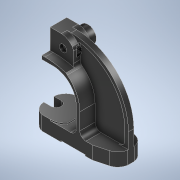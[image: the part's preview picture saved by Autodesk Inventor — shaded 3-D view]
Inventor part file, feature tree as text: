
AUTODESK INVENTOR PART (.ipt)
format: ipt  version: 2021 (Build 250183000, 183)  size: 490,496 bytes
history: native  units: in
note: dims shown in document units (in); Inventor stores cm internally (conversion verified against a paired STEP export)
features: sketch x18, extrude x17, mirror x3, fillet x3, plane x1, hole x1, projected_geometry x1
ambient origin geometry x8: Origin, YZ Plane, XZ Plane, XY Plane, X Axis, Y Axis, Z Axis, Center Point
bodies: Solid1 (feature_tree)
feature tree (44):
  extrude  "Extrusion1"  Depth=1.5in
  extrude  "Extrusion2"  Depth=2.5in
  extrude  "Extrusion3"  Depth=9.0in
  extrude  "Extrusion4"  Depth=0.125in
  extrude  "Extrusion5"  Depth=1.5in
  plane  "Work Plane1"
  mirror  "Mirror1"
  extrude  "Extrusion6"  Depth=3.5in TaperAngle=0.0deg
  extrude  "Extrusion7"  TaperAngle=15.0deg  [1 undecoded]
  extrude  "Extrusion8"  TaperAngle=0.0deg  [1 undecoded]
  extrude  "Extrusion9"  Depth=2.434in
  extrude  "Extrusion10"  Depth=3.375in
  extrude  "Extrusion11"  Depth=0.375in
  mirror  "Mirror2"
  fillet  "Fillet1"  Radius=0.125in
  extrude  "Extrusion12"  Depth=0.375in
  extrude  "Extrusion13"  Depth=0.875in TaperAngle=0.0deg
  mirror  "Mirror3"
  fillet  "Fillet2"  Radius=1.75in
  extrude  "Extrusion14"  Depth=0.875in TaperAngle=0.0deg
  extrude  "Extrusion15"  Depth=0.875in
  extrude  "Extrusion16"  Depth=0.5in
  extrude  "Extrusion17"  Depth=1.375in
  fillet  "Fillet3"  Radius=1.375in
  hole  "Hole1"  [1 undecoded]
  sketch  "Sketch1"  dims[d0=8.625in d1=1.5in]
  sketch  "Sketch2"  dims[d2=3.125in d3=2.5in]
  sketch  "Sketch3"  dims[d4=1.184in d5=9.0in]
  sketch  "Sketch4"  dims[d6=1.0in d7=0.125in]
  sketch  "Sketch5"  dims[d8=1.5in d10=7.5948in]
  sketch  "Sketch6"  dims[d11=6.0in d12=3.5in d13=0.0in]
  sketch  "Sketch7"  dims[d14=1.25in d15=15.0deg]
  sketch  "Sketch8"  dims[d16=1.312in d17=0.0in d18=0.0in]
  sketch  "Sketch9"  dims[d19=2.434in d20=2.365in]
  sketch  "Sketch10"  dims[d21=0.37in d22=3.375in]
  sketch  "Sketch11"  dims[d23=1.469in d24=0.0in d25=0.375in d26=0.125in d27=0.0in]
  sketch  "Sketch12"  dims[d28=1.75in d30=0.375in]
  sketch  "Sketch13"  dims[d31=0.125in d32=0.875in d33=0.0in d35=1.75in]
  sketch  "Sketch14"  dims[d36=0.375in d37=0.875in d38=0.0in]
  projected_geometry  "Projected Loop1"
  sketch  "Sketch15"  dims[d39=0.875in d40=0.0in d41=1.84in]
  sketch  "Sketch16"  dims[d42=0.75in d43=0.5in]
  sketch  "Sketch17"  dims[d44=1.0in d45=0.0in d46=1.172in d47=1.375in d48=0.0in]
  sketch  "Sketch18"  dims[d49=0.75in d50=1.375in d51=0.0in d52=1.25in d53=0.594in d54=0.0in d55=0.625in d56=0.75in d57=0.5315in d58=0.0in d59=0.0in d60=1.25in d61=0.525in d62=1.75in d63=0.125in d64=0.0in d65=0.625in d66=0.312in d67=1.1875in d68=0.0in d69=2.562in d70=0.125in d71=5.562in d72=0.0in d73=0.0in d75=3.0in d76=0.5in d77=0.0in d78=30.0deg d79=2.876in d80=0.0in d81=0.125in d82=1.25in d83=0.25in d84=0.0849in d85=0.5in d86=0.375in d87=0.25in d88=0.5635in d89=0.752in d90=0.8108in]
note: 3 required parameter values undecoded (feature->parameter linkage not recoverable at this tier; creation-order binding heuristic only, values carry confidence <= 0.55)
